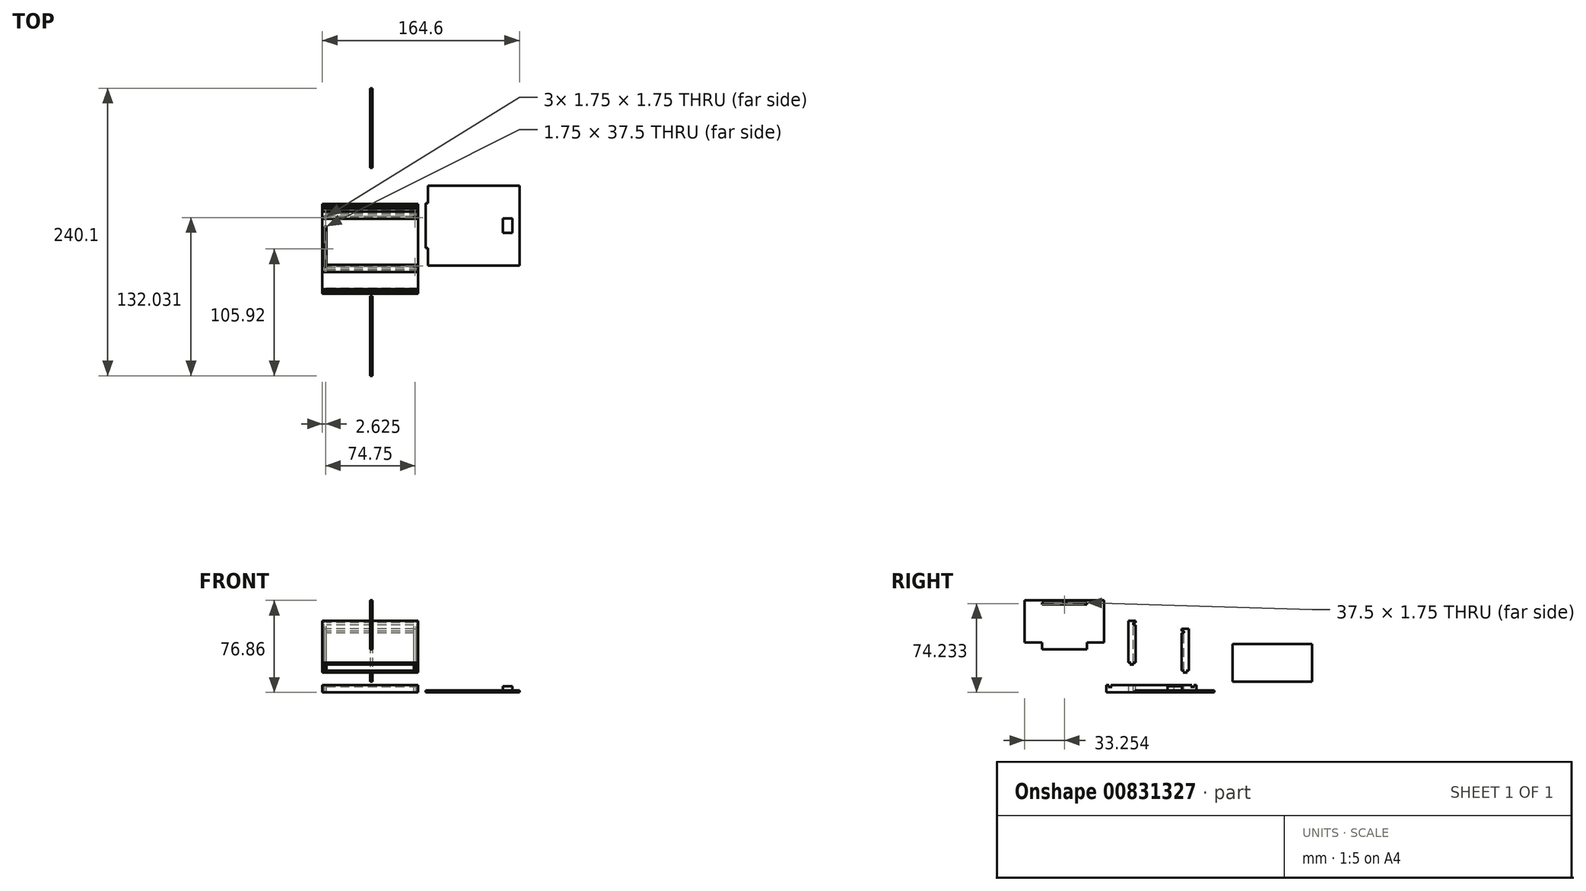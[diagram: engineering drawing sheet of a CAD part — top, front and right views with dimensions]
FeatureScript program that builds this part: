
annotation { "Feature Type Name" : "Feature", "Feature Type Description" : "" }
export const myFeature = defineFeature(function(context is Context, id is Id, definition is map)
    precondition{}
    {
        {
            assignVariable(context, id + "F0", {"name" : "BoxW", "anyValue" : 80});
        }
        {
            assignVariable(context, id + "F1", {"name" : "Thickness", "anyValue" : 6});
        }
        {
            assignVariable(context, id + "F2", {"name" : "Groove", "anyValue" : 1.75});
        }
        {
            var Q0;
            Q0=qCreatedBy(makeId("Right.planeOp"),FACE);
            var sketch = newSketch(context, id + "F3", { "sketchPlane" : qUnion([Q0])});
            skLineSegment(sketch, "E0", {"start": v(0, 0) * mm, "end": v(0, 11.57) * mm, "construction": true});
            skLineSegment(sketch, "E1", {"start": v(-37.5, 0) * mm, "end": v(37.5, 0) * mm});
            skLineSegment(sketch, "E2", {"start": v(37.5, 0) * mm, "end": v(37.5, 6) * mm});
            skLineSegment(sketch, "E3", {"start": v(37.5, 6) * mm, "end": v(35.25, 6) * mm});
            skLineSegment(sketch, "E4", {"start": v(35.25, 6) * mm, "end": v(36.12, 4.5) * mm});
            skLineSegment(sketch, "E5", {"start": v(36.12, 4.5) * mm, "end": v(32.88, 4.5) * mm});
            skLineSegment(sketch, "E6", {"start": v(32.88, 4.5) * mm, "end": v(33.75, 6) * mm});
            skLineSegment(sketch, "E7", {"start": v(33.75, 6) * mm, "end": v(-33.75, 6) * mm});
            skLineSegment(sketch, "E8", {"start": v(-33.75, 6) * mm, "end": v(-32.88, 4.5) * mm});
            skLineSegment(sketch, "E9", {"start": v(-32.88, 4.5) * mm, "end": v(-36.12, 4.5) * mm});
            skLineSegment(sketch, "E10", {"start": v(-36.12, 4.5) * mm, "end": v(-35.25, 6) * mm});
            skLineSegment(sketch, "E11", {"start": v(-35.25, 6) * mm, "end": v(-37.5, 6) * mm});
            skLineSegment(sketch, "E12", {"start": v(-37.5, 6) * mm, "end": v(-37.5, 0) * mm});
            skLineSegment(sketch, "E13", {"start": v(-31.5, -2.32) * mm, "end": v(-31.5, 5.5) * mm, "construction": true});
            skLineSegment(sketch, "E14", {"start": v(31.5, -1.94) * mm, "end": v(31.5, 9.5) * mm, "construction": true});
            skLineSegment(sketch, "E15", {"start": v(34.5, 8.68) * mm, "end": v(34.5, -2.27) * mm, "construction": true});
            skPoint(sketch, "E15.startSnap0", {"position": v(34.5, 4.5) * mm});
            skLineSegment(sketch, "E16", {"start": v(-34.5, -0.73) * mm, "end": v(-34.5, 9.07) * mm, "construction": true});
            skSolve(sketch);
        }
        {
            var Q0;
            Q0=makeQuery(id+"F3.imprint","IMPRINT",FACE,{"disambiguationData":[TD([[makeQuery(id+"F3.imprint","IMPRINT",EDGE,{"derivedFrom":sQuery(id+"F3.wireOp",EDGE,"E1")}),1.0]])]});
            extrude(context, id + "F4", {"entities" : qUnion([Q0]), "depth" : (getVariable(context, 'BoxW')) * mm, "offsetDistance" : 25 * mm, "symmetric" : true});
        }
        {
            var Q0;
            Q0=makeQuery(id+"F4.opExtrude","SWEPT_FACE",FACE,{"disambiguationData":[OSD([sQuery(id+"F3.wireOp",EDGE,"E7")])]});
            var sketch = newSketch(context, id + "F5", { "sketchPlane" : qUnion([Q0])});
            skLineSegment(sketch, "E17.bottom", {"start": v(-36.5, 18.75) * mm, "end": v(-38.25, 18.75) * mm});
            skLineSegment(sketch, "E17.top", {"start": v(-36.5, -18.75) * mm, "end": v(-38.25, -18.75) * mm});
            skLineSegment(sketch, "E17.left", {"start": v(-36.5, 18.75) * mm, "end": v(-36.5, -18.75) * mm});
            skLineSegment(sketch, "E17.right", {"start": v(-38.25, 18.75) * mm, "end": v(-38.25, -18.75) * mm});
            skPoint(sketch, "E17.middle", {"position": v(-37.38, 0) * mm});
            skPoint(sketch, "E17.middle.positionSnap0", {"position": v(-40, 0) * mm});
            skPoint(sketch, "E17.centerSnap0", {"position": v(-40, 0) * mm});
            skSolve(sketch);
        }
        {
            var Q0;
            Q0=makeQuery(id+"F5.imprint","IMPRINT",FACE,{"disambiguationData":[TD([[makeQuery(id+"F5.imprint","IMPRINT",EDGE,{"derivedFrom":sQuery(id+"F5.wireOp",EDGE,"E17.bottom")}),1.0]])]});
            extrude(context, id + "F6", {"entities" : qUnion([Q0]), "operationType" : NewBodyOperationType.REMOVE, "endBound" : BoundingType.THROUGH_ALL, "oppositeDirection" : true, "depth" : 25 * mm, "offsetDistance" : 25 * mm});
        }
        {
            var Q0;
            Q0=qCreatedBy(makeId("Right.planeOp"),FACE);
            var sketch = newSketch(context, id + "F7", { "sketchPlane" : qUnion([Q0])});
            skLineSegment(sketch, "E18", {"start": v(-19.26, 59.87) * mm, "end": v(-19.26, 24.87) * mm});
            skLineSegment(sketch, "E19", {"start": v(-19.26, 24.87) * mm, "end": v(-17, 24.87) * mm});
            skLineSegment(sketch, "E20", {"start": v(-17, 24.87) * mm, "end": v(-17.87, 23.37) * mm});
            skLineSegment(sketch, "E21", {"start": v(-17.87, 23.37) * mm, "end": v(-14.64, 23.37) * mm});
            skLineSegment(sketch, "E22", {"start": v(-14.64, 23.37) * mm, "end": v(-15.5, 24.87) * mm});
            skLineSegment(sketch, "E23", {"start": v(-15.5, 24.87) * mm, "end": v(-13.26, 24.87) * mm});
            skLineSegment(sketch, "E24", {"start": v(-13.26, 24.87) * mm, "end": v(-13.26, 56.37) * mm});
            skLineSegment(sketch, "E25", {"start": v(-13.26, 56.37) * mm, "end": v(-15, 56.37) * mm});
            skLineSegment(sketch, "E26", {"start": v(-15, 56.37) * mm, "end": v(-15, 58.12) * mm});
            skLineSegment(sketch, "E27", {"start": v(-15, 58.12) * mm, "end": v(-13.26, 58.12) * mm});
            skLineSegment(sketch, "E28", {"start": v(-13.26, 58.12) * mm, "end": v(-13.26, 59.87) * mm});
            skLineSegment(sketch, "E29", {"start": v(-13.26, 59.87) * mm, "end": v(-19.26, 59.87) * mm});
            skLineSegment(sketch, "E30", {"start": v(-16.26, 23.37) * mm, "end": v(-16.26, 61.37) * mm, "construction": true});
            skSolve(sketch);
        }
        {
            var Q0;
            Q0=makeQuery(id+"F7.imprint","IMPRINT",FACE,{"disambiguationData":[TD([[makeQuery(id+"F7.imprint","IMPRINT",EDGE,{"derivedFrom":sQuery(id+"F7.wireOp",EDGE,"E18")}),1.0]])]});
            extrude(context, id + "F8", {"entities" : qUnion([Q0]), "depth" : (getVariable(context, 'BoxW')) * mm, "offsetDistance" : 25 * mm, "symmetric" : true});
        }
        {
            var Q0;
            Q0=makeQuery(id+"F8.opExtrude","SWEPT_FACE",FACE,{"disambiguationData":[OSD([sQuery(id+"F7.wireOp",EDGE,"E29")])]});
            var sketch = newSketch(context, id + "F9", { "sketchPlane" : qUnion([Q0])});
            skLineSegment(sketch, "E31.bottom", {"start": v(-38.25, -13.26) * mm, "end": v(-36.5, -13.26) * mm});
            skLineSegment(sketch, "E31.top", {"start": v(-38.25, -15) * mm, "end": v(-36.5, -15) * mm});
            skLineSegment(sketch, "E31.left", {"start": v(-38.25, -13.26) * mm, "end": v(-38.25, -15) * mm});
            skLineSegment(sketch, "E31.right", {"start": v(-36.5, -13.26) * mm, "end": v(-36.5, -15) * mm});
            skLineSegment(sketch, "E32.bottom", {"start": v(36.5, -13.26) * mm, "end": v(38.25, -13.26) * mm});
            skLineSegment(sketch, "E32.top", {"start": v(36.5, -15) * mm, "end": v(38.25, -15) * mm});
            skLineSegment(sketch, "E32.left", {"start": v(36.5, -13.26) * mm, "end": v(36.5, -15) * mm});
            skLineSegment(sketch, "E32.right", {"start": v(38.25, -13.26) * mm, "end": v(38.25, -15) * mm});
            skSolve(sketch);
        }
        {
            var Q0;
            Q0=makeQuery(id+"F9.imprint","IMPRINT",FACE,{"disambiguationData":[TD([[makeQuery(id+"F9.imprint","IMPRINT",EDGE,{"derivedFrom":sQuery(id+"F9.wireOp",EDGE,"E31.bottom")}),1.0]])]});
            var Q1;
            Q1=makeQuery(id+"F9.imprint","IMPRINT",FACE,{"disambiguationData":[TD([[makeQuery(id+"F9.imprint","IMPRINT",EDGE,{"derivedFrom":sQuery(id+"F9.wireOp",EDGE,"E32.bottom")}),1.0]])]});
            extrude(context, id + "F10", {"entities" : qUnion([Q0, Q1]), "operationType" : NewBodyOperationType.REMOVE, "endBound" : BoundingType.THROUGH_ALL, "oppositeDirection" : true, "depth" : 25 * mm, "offsetDistance" : 25 * mm});
        }
        {
            var Q0;
            Q0=qCreatedBy(makeId("Right.planeOp"),FACE);
            var sketch = newSketch(context, id + "F11", { "sketchPlane" : qUnion([Q0])});
            skLineSegment(sketch, "E33", {"start": v(25.24, 53.08) * mm, "end": v(25.24, 51.33) * mm});
            skLineSegment(sketch, "E34", {"start": v(25.24, 18.08) * mm, "end": v(27.49, 18.08) * mm});
            skLineSegment(sketch, "E35", {"start": v(27.49, 18.08) * mm, "end": v(26.62, 16.58) * mm});
            skLineSegment(sketch, "E36", {"start": v(26.62, 16.58) * mm, "end": v(29.85, 16.58) * mm});
            skLineSegment(sketch, "E37", {"start": v(29.85, 16.58) * mm, "end": v(28.99, 18.08) * mm});
            skLineSegment(sketch, "E38", {"start": v(28.99, 18.08) * mm, "end": v(31.24, 18.08) * mm});
            skLineSegment(sketch, "E39", {"start": v(31.24, 18.08) * mm, "end": v(31.24, 53.08) * mm});
            skLineSegment(sketch, "E40", {"start": v(31.24, 53.08) * mm, "end": v(25.24, 53.08) * mm});
            skLineSegment(sketch, "E41", {"start": v(28.24, 16.58) * mm, "end": v(28.24, 68.66) * mm, "construction": true});
            skLineSegment(sketch, "E42", {"start": v(25.24, 51.33) * mm, "end": v(26.99, 51.33) * mm});
            skLineSegment(sketch, "E43", {"start": v(26.99, 51.33) * mm, "end": v(26.99, 49.58) * mm});
            skLineSegment(sketch, "E44", {"start": v(26.99, 49.58) * mm, "end": v(25.24, 49.58) * mm});
            skLineSegment(sketch, "E45", {"start": v(25.24, 49.58) * mm, "end": v(25.24, 18.08) * mm});
            skSolve(sketch);
        }
        {
            var Q0;
            Q0=makeQuery(id+"F11.imprint","IMPRINT",FACE,{"disambiguationData":[TD([[makeQuery(id+"F11.imprint","IMPRINT",EDGE,{"derivedFrom":sQuery(id+"F11.wireOp",EDGE,"E33")}),1.0]])]});
            extrude(context, id + "F12", {"entities" : qUnion([Q0]), "depth" : (getVariable(context, 'BoxW')) * mm, "offsetDistance" : 25 * mm, "symmetric" : true});
        }
        {
            var Q0;
            Q0=makeQuery(id+"F12.opExtrude","SWEPT_FACE",FACE,{"disambiguationData":[OSD([sQuery(id+"F11.wireOp",EDGE,"E40")])]});
            var sketch = newSketch(context, id + "F13", { "sketchPlane" : qUnion([Q0])});
            skLineSegment(sketch, "E46.bottom", {"start": v(-38.25, 25.24) * mm, "end": v(-36.5, 25.24) * mm});
            skLineSegment(sketch, "E46.top", {"start": v(-38.25, 26.99) * mm, "end": v(-36.5, 26.99) * mm});
            skLineSegment(sketch, "E46.left", {"start": v(-38.25, 25.24) * mm, "end": v(-38.25, 26.99) * mm});
            skLineSegment(sketch, "E46.right", {"start": v(-36.5, 25.24) * mm, "end": v(-36.5, 26.99) * mm});
            skLineSegment(sketch, "E47.bottom", {"start": v(36.5, 25.24) * mm, "end": v(38.25, 25.24) * mm});
            skLineSegment(sketch, "E47.top", {"start": v(36.5, 26.99) * mm, "end": v(38.25, 26.99) * mm});
            skLineSegment(sketch, "E47.left", {"start": v(36.5, 25.24) * mm, "end": v(36.5, 26.99) * mm});
            skLineSegment(sketch, "E47.right", {"start": v(38.25, 25.24) * mm, "end": v(38.25, 26.99) * mm});
            skSolve(sketch);
        }
        {
            var Q0;
            Q0=makeQuery(id+"F13.imprint","IMPRINT",FACE,{"disambiguationData":[TD([[makeQuery(id+"F13.imprint","IMPRINT",EDGE,{"derivedFrom":sQuery(id+"F13.wireOp",EDGE,"E46.bottom")}),-1.0]])]});
            var Q1;
            Q1=makeQuery(id+"F13.imprint","IMPRINT",FACE,{"disambiguationData":[TD([[makeQuery(id+"F13.imprint","IMPRINT",EDGE,{"derivedFrom":sQuery(id+"F13.wireOp",EDGE,"E47.bottom")}),-1.0]])]});
            extrude(context, id + "F14", {"entities" : qUnion([Q0, Q1]), "operationType" : NewBodyOperationType.REMOVE, "endBound" : BoundingType.THROUGH_ALL, "oppositeDirection" : true, "depth" : 25 * mm, "offsetDistance" : 25 * mm});
        }
        {
            var Q0;
            Q0=qCreatedBy(makeId("Right.planeOp"),FACE);
            var sketch = newSketch(context, id + "F15", { "sketchPlane" : qUnion([Q0])});
            skLineSegment(sketch, "E48.bottom", {"start": v(-105.92, 76.86) * mm, "end": v(-39.42, 76.86) * mm});
            skLineSegment(sketch, "E48.top", {"start": v(-105.92, 41.86) * mm, "end": v(-39.42, 41.86) * mm});
            skLineSegment(sketch, "E48.left", {"start": v(-105.92, 76.86) * mm, "end": v(-105.92, 41.86) * mm});
            skLineSegment(sketch, "E48.right", {"start": v(-39.42, 76.86) * mm, "end": v(-39.42, 41.86) * mm});
            skSolve(sketch);
        }
        {
            var Q0;
            Q0=makeQuery(id+"F15.imprint","IMPRINT",FACE,{"disambiguationData":[TD([[makeQuery(id+"F15.imprint","IMPRINT",EDGE,{"derivedFrom":sQuery(id+"F15.wireOp",EDGE,"E48.bottom")}),-1.0]])]});
            extrude(context, id + "F16", {"entities" : qUnion([Q0]), "depth" : (getVariable(context, 'Groove')) * mm, "offsetDistance" : 25 * mm});
        }
        {
            var Q0;
            Q0=makeQuery(id+"F16.opExtrude","SWEPT_FACE",FACE,{"disambiguationData":[OSD([sQuery(id+"F15.wireOp",EDGE,"E48.top")])]});
            var sketch = newSketch(context, id + "F17", { "sketchPlane" : qUnion([Q0])});
            skLineSegment(sketch, "E49.bottom", {"start": v(0, 53.92) * mm, "end": v(1.75, 53.92) * mm});
            skLineSegment(sketch, "E49.top", {"start": v(0, 91.42) * mm, "end": v(1.75, 91.42) * mm});
            skLineSegment(sketch, "E49.left", {"start": v(0, 53.92) * mm, "end": v(0, 91.42) * mm});
            skLineSegment(sketch, "E49.right", {"start": v(1.75, 53.92) * mm, "end": v(1.75, 91.42) * mm});
            skPoint(sketch, "E49.middle", {"position": v(0.88, 72.67) * mm});
            skPoint(sketch, "E49.middle.positionSnap0", {"position": v(0.88, 105.92) * mm});
            skPoint(sketch, "E49.middle.positionSnap1", {"position": v(0, 72.67) * mm});
            skPoint(sketch, "E49.centerSnap0", {"position": v(0.88, 105.92) * mm});
            skPoint(sketch, "E49.centerSnap1", {"position": v(0, 72.67) * mm});
            skSolve(sketch);
        }
        {
            var Q0;
            Q0=makeQuery(id+"F17.imprint","IMPRINT",FACE,{"disambiguationData":[TD([[makeQuery(id+"F17.imprint","IMPRINT",EDGE,{"derivedFrom":sQuery(id+"F17.wireOp",EDGE,"E49.bottom")}),1.0]])]});
            extrude(context, id + "F18", {"entities" : qUnion([Q0]), "operationType" : NewBodyOperationType.ADD, "depth" : (getVariable(context, 'Thickness')) * mm, "offsetDistance" : 25 * mm});
        }
        {
            var Q0;
            Q0=makeQuery(id+"F18.boolean.opBoolean","MERGE",FACE,{"derivedFrom":[makeQuery(id+"F16.opExtrude","CAP_FACE",FACE,{"disambiguationData":[OSD([sQuery(id+"F15.wireOp",EDGE,"E48.bottom"),sQuery(id+"F15.wireOp",EDGE,"E48.top"),sQuery(id+"F15.wireOp",EDGE,"E48.left"),sQuery(id+"F15.wireOp",EDGE,"E48.right")])],"isStart":false}),makeQuery(id+"F18.opExtrude","SWEPT_FACE",FACE,{"disambiguationData":[OSD([sQuery(id+"F17.wireOp",EDGE,"E49.right")])]})]});
            var sketch = newSketch(context, id + "F19", { "sketchPlane" : qUnion([Q0])});
            skLineSegment(sketch, "E50.bottom", {"start": v(-53.92, 73.36) * mm, "end": v(-91.42, 73.36) * mm});
            skLineSegment(sketch, "E50.top", {"start": v(-53.92, 75.1) * mm, "end": v(-91.42, 75.1) * mm});
            skLineSegment(sketch, "E50.left", {"start": v(-53.92, 73.36) * mm, "end": v(-53.92, 75.1) * mm});
            skLineSegment(sketch, "E50.right", {"start": v(-91.42, 73.36) * mm, "end": v(-91.42, 75.1) * mm});
            skPoint(sketch, "E50.middle", {"position": v(-72.67, 74.23) * mm});
            skPoint(sketch, "E50.middle.positionSnap0", {"position": v(-72.67, 76.86) * mm});
            skPoint(sketch, "E50.centerSnap0", {"position": v(-72.67, 76.86) * mm});
            skSolve(sketch);
        }
        {
            var Q0;
            Q0=makeQuery(id+"F19.imprint","IMPRINT",FACE,{"disambiguationData":[TD([[makeQuery(id+"F19.imprint","IMPRINT",EDGE,{"derivedFrom":sQuery(id+"F19.wireOp",EDGE,"E50.bottom")}),-1.0]])]});
            extrude(context, id + "F20", {"entities" : qUnion([Q0]), "operationType" : NewBodyOperationType.REMOVE, "endBound" : BoundingType.THROUGH_ALL, "oppositeDirection" : true, "depth" : 25 * mm, "offsetDistance" : 25 * mm});
        }
        {
            var Q0;
            Q0=qCreatedBy(makeId("Right.planeOp"),FACE);
            var sketch = newSketch(context, id + "F21", { "sketchPlane" : qUnion([Q0])});
            skLineSegment(sketch, "E51.bottom", {"start": v(67.68, 40.36) * mm, "end": v(134.18, 40.36) * mm});
            skLineSegment(sketch, "E51.top", {"start": v(67.68, 8.86) * mm, "end": v(134.18, 8.86) * mm});
            skLineSegment(sketch, "E51.left", {"start": v(67.68, 40.36) * mm, "end": v(67.68, 8.86) * mm});
            skLineSegment(sketch, "E51.right", {"start": v(134.18, 40.36) * mm, "end": v(134.18, 8.86) * mm});
            skSolve(sketch);
        }
        {
            var Q0;
            Q0=makeQuery(id+"F21.imprint","IMPRINT",FACE,{"disambiguationData":[TD([[makeQuery(id+"F21.imprint","IMPRINT",EDGE,{"derivedFrom":sQuery(id+"F21.wireOp",EDGE,"E51.bottom")}),-1.0]])]});
            extrude(context, id + "F22", {"entities" : qUnion([Q0]), "depth" : (getVariable(context, 'Groove')) * mm, "offsetDistance" : 25 * mm});
        }
        {
            var Q0;
            Q0=qCreatedBy(makeId("Top.planeOp"),FACE);
            var sketch = newSketch(context, id + "F23", { "sketchPlane" : qUnion([Q0])});
            skLineSegment(sketch, "E52.bottom", {"start": v(48.1, -13.82) * mm, "end": v(124.6, -13.82) * mm});
            skLineSegment(sketch, "E52.top", {"start": v(48.1, 52.68) * mm, "end": v(124.6, 52.68) * mm});
            skLineSegment(sketch, "E52.left", {"start": v(48.1, -13.82) * mm, "end": v(48.1, 52.68) * mm});
            skLineSegment(sketch, "E52.right", {"start": v(124.6, -13.82) * mm, "end": v(124.6, 52.68) * mm});
            skSolve(sketch);
        }
        {
            var Q0;
            Q0=makeQuery(id+"F23.imprint","IMPRINT",FACE,{"disambiguationData":[TD([[makeQuery(id+"F23.imprint","IMPRINT",EDGE,{"derivedFrom":sQuery(id+"F23.wireOp",EDGE,"E52.bottom")}),1.0]])]});
            extrude(context, id + "F24", {"entities" : qUnion([Q0]), "depth" : (getVariable(context, 'Groove')) * mm, "offsetDistance" : 25 * mm});
        }
        {
            var Q0;
            Q0=makeQuery(id+"F24.opExtrude","SWEPT_FACE",FACE,{"disambiguationData":[OSD([sQuery(id+"F23.wireOp",EDGE,"E52.left")])]});
            var sketch = newSketch(context, id + "F25", { "sketchPlane" : qUnion([Q0])});
            skLineSegment(sketch, "E53.bottom", {"start": v(-0.68, 0) * mm, "end": v(-38.18, 0) * mm});
            skLineSegment(sketch, "E53.top", {"start": v(-0.68, 1.75) * mm, "end": v(-38.18, 1.75) * mm});
            skLineSegment(sketch, "E53.left", {"start": v(-0.68, 0) * mm, "end": v(-0.68, 1.75) * mm});
            skLineSegment(sketch, "E53.right", {"start": v(-38.18, 0) * mm, "end": v(-38.18, 1.75) * mm});
            skPoint(sketch, "E53.middle", {"position": v(-19.43, 0.88) * mm});
            skPoint(sketch, "E53.middle.positionSnap0", {"position": v(-19.43, 0) * mm});
            skPoint(sketch, "E53.middle.positionSnap1", {"position": v(-52.68, 0.88) * mm});
            skPoint(sketch, "E53.centerSnap0", {"position": v(-19.43, 0) * mm});
            skPoint(sketch, "E53.centerSnap1", {"position": v(-52.68, 0.88) * mm});
            skSolve(sketch);
        }
        {
            var Q0;
            Q0=makeQuery(id+"F25.imprint","IMPRINT",FACE,{"disambiguationData":[TD([[makeQuery(id+"F25.imprint","IMPRINT",EDGE,{"derivedFrom":sQuery(id+"F25.wireOp",EDGE,"E53.bottom")}),-1.0]])]});
            extrude(context, id + "F26", {"entities" : qUnion([Q0]), "operationType" : NewBodyOperationType.ADD, "depth" : (getVariable(context, 'Groove')) * mm, "offsetDistance" : 25 * mm});
        }
        {
            var Q0;
            Q0=makeQuery(id+"F24.opExtrude","CAP_FACE",FACE,{"disambiguationData":[OSD([sQuery(id+"F23.wireOp",EDGE,"E52.bottom"),sQuery(id+"F23.wireOp",EDGE,"E52.top"),sQuery(id+"F23.wireOp",EDGE,"E52.left"),sQuery(id+"F23.wireOp",EDGE,"E52.right")])],"isStart":false});
            var sketch = newSketch(context, id + "F27", { "sketchPlane" : qUnion([Q0])});
            skLineSegment(sketch, "E54.bottom", {"start": v(118.6, 25.43) * mm, "end": v(110.6, 25.43) * mm});
            skLineSegment(sketch, "E54.top", {"start": v(118.6, 13.43) * mm, "end": v(110.6, 13.43) * mm});
            skLineSegment(sketch, "E54.left", {"start": v(118.6, 25.43) * mm, "end": v(118.6, 13.43) * mm});
            skLineSegment(sketch, "E54.right", {"start": v(110.6, 25.43) * mm, "end": v(110.6, 13.43) * mm});
            skPoint(sketch, "E54.middle", {"position": v(114.6, 19.43) * mm});
            skPoint(sketch, "E54.middle.positionSnap0", {"position": v(124.6, 19.43) * mm});
            skPoint(sketch, "E54.centerSnap0", {"position": v(124.6, 19.43) * mm});
            skSolve(sketch);
        }
        {
            var Q0;
            Q0=makeQuery(id+"F27.imprint","IMPRINT",FACE,{"disambiguationData":[TD([[makeQuery(id+"F27.imprint","IMPRINT",EDGE,{"derivedFrom":sQuery(id+"F27.wireOp",EDGE,"E54.bottom")}),1.0]])]});
            extrude(context, id + "F28", {"entities" : qUnion([Q0]), "operationType" : NewBodyOperationType.ADD, "depth" : (getVariable(context, 'Groove') * 2) * mm, "offsetDistance" : 25 * mm});
        }
    });
